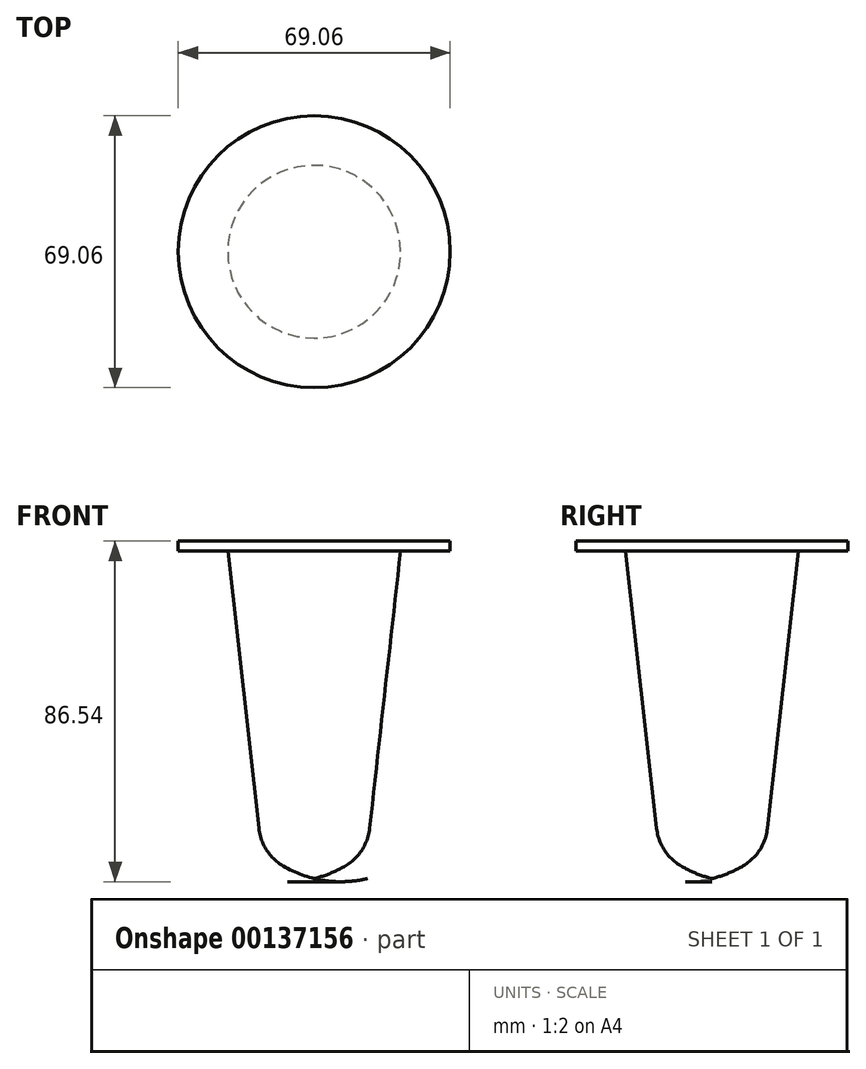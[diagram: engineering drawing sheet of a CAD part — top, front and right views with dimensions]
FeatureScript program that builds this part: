
annotation { "Feature Type Name" : "Feature", "Feature Type Description" : "" }
export const myFeature = defineFeature(function(context is Context, id is Id, definition is map)
    precondition{}
    {
        {
            var Q0;
            Q0=qCreatedBy(makeId("Front.planeOp"),FACE);
            var sketch = newSketch(context, id + "F0", { "sketchPlane" : qUnion([Q0])});
            skArc(sketch, "E0", {"start": v(-13.48, 7.48) * mm, "mid": v(-7.25, 2.83) * mm, "end": v(0, 0) * mm});
            skLineSegment(sketch, "E1", {"start": v(-13.48, 7.48) * mm, "end": v(-21.94, 83.19) * mm});
            skLineSegment(sketch, "E2", {"start": v(-21.94, 83.19) * mm, "end": v(0, 83.19) * mm});
            skLineSegment(sketch, "E3", {"start": v(0, 83.19) * mm, "end": v(0, 0) * mm});
            skSolve(sketch);
        }
        {
            var Q0;
            Q0 = qSketchRegion(id + "F0", true);
            var Q1;
            Q1=sQuery(id+"F0.wireOp",EDGE,"E3");
            revolve(context, id + "F1", {"entities" : qUnion([Q0]), "axis" : qUnion([Q1]), "revolveType" : RevolveType.FULL});
        }
        {
            var Q0;
            Q0=makeQuery(id+"F1.opRevolve","SWEPT_EDGE",EDGE,{"disambiguationData":[OSD([sQuery(id+"F0.wireOp",EDGE,"E0"),sQuery(id+"F0.wireOp",EDGE,"E1")])]});
            fillet(context, id + "F2", {"entities" : qUnion([Q0]), "radius" : 12.7 * mm, "tangentPropagation" : true, "allowEdgeOverflow" : false});
        }
        {
            var Q0;
            Q0=makeQuery(id+"F1.opRevolve","SWEPT_FACE",FACE,{"disambiguationData":[OSD([sQuery(id+"F0.wireOp",EDGE,"E2")])]});
            var sketch = newSketch(context, id + "F3", { "sketchPlane" : qUnion([Q0])});
            skCircle(sketch, "E4", {"center": v(0, 0) * mm, "radius": 34.53 * mm});
            skSolve(sketch);
        }
        {
            var Q0;
            Q0 = qSketchRegion(id + "F3", true);
            extrude(context, id + "F4", {"entities" : qUnion([Q0]), "operationType" : NewBodyOperationType.ADD, "depth" : 2.54 * mm});
        }
    });
